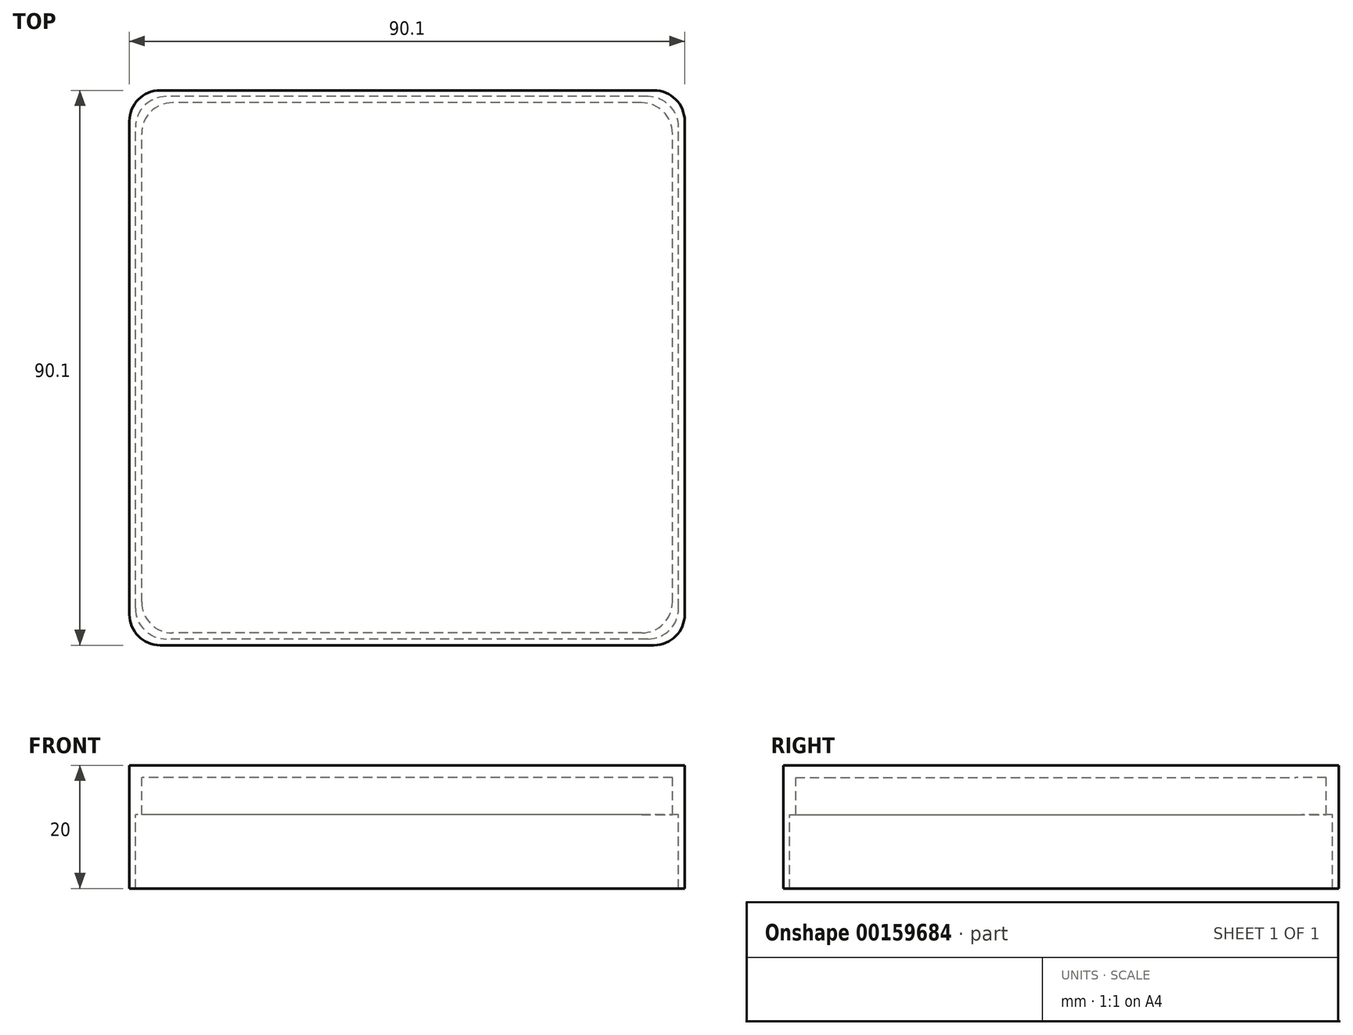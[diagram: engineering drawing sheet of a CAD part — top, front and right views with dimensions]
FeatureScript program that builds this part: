
annotation { "Feature Type Name" : "Feature", "Feature Type Description" : "" }
export const myFeature = defineFeature(function(context is Context, id is Id, definition is map)
    precondition{}
    {
        {
            var Q0;
            Q0=qCreatedBy(makeId("Top.planeOp"),FACE);
            var sketch = newSketch(context, id + "F0", { "sketchPlane" : qUnion([Q0])});
            skLineSegment(sketch, "E0.bottom", {"start": v(45.05, -45.05) * mm, "end": v(-45.05, -45.05) * mm});
            skLineSegment(sketch, "E0.top", {"start": v(45.05, 45.05) * mm, "end": v(-45.05, 45.05) * mm});
            skLineSegment(sketch, "E0.left", {"start": v(45.05, -45.05) * mm, "end": v(45.05, 45.05) * mm});
            skLineSegment(sketch, "E0.right", {"start": v(-45.05, -45.05) * mm, "end": v(-45.05, 45.05) * mm});
            skPoint(sketch, "E0.middle", {"position": v(0, 0) * mm});
            skLineSegment(sketch, "E1.bottom", {"start": v(44.05, -44.05) * mm, "end": v(-44.05, -44.05) * mm});
            skLineSegment(sketch, "E1.top", {"start": v(44.05, 44.05) * mm, "end": v(-44.05, 44.05) * mm});
            skLineSegment(sketch, "E1.left", {"start": v(44.05, -44.05) * mm, "end": v(44.05, 44.05) * mm});
            skLineSegment(sketch, "E1.right", {"start": v(-44.05, -44.05) * mm, "end": v(-44.05, 44.05) * mm});
            skLineSegment(sketch, "E2.bottom", {"start": v(43.05, -43.05) * mm, "end": v(-43.05, -43.05) * mm});
            skLineSegment(sketch, "E2.top", {"start": v(43.05, 43.05) * mm, "end": v(-43.05, 43.05) * mm});
            skLineSegment(sketch, "E2.left", {"start": v(43.05, -43.05) * mm, "end": v(43.05, 43.05) * mm});
            skLineSegment(sketch, "E2.right", {"start": v(-43.05, -43.05) * mm, "end": v(-43.05, 43.05) * mm});
            skSolve(sketch);
        }
        {
            var Q0;
            Q0=makeQuery(id+"F0.imprint","IMPRINT",FACE,{"disambiguationData":[TD([[makeQuery(id+"F0.imprint","IMPRINT",EDGE,{"derivedFrom":sQuery(id+"F0.wireOp",EDGE,"E2.bottom")}),-1.0]])]});
            extrude(context, id + "F1", {"entities" : qUnion([Q0]), "oppositeDirection" : true, "depth" : 2 * mm});
        }
        {
            var Q0;
            Q0=makeQuery(id+"F0.imprint","IMPRINT",FACE,{"disambiguationData":[TD([[makeQuery(id+"F0.imprint","IMPRINT",EDGE,{"derivedFrom":sQuery(id+"F0.wireOp",EDGE,"E1.bottom")}),-1.0]])]});
            extrude(context, id + "F2", {"entities" : qUnion([Q0]), "operationType" : NewBodyOperationType.ADD, "oppositeDirection" : true, "depth" : 8 * mm});
        }
        {
            var Q0;
            Q0=makeQuery(id+"F0.imprint","IMPRINT",FACE,{"disambiguationData":[TD([[makeQuery(id+"F0.imprint","IMPRINT",EDGE,{"derivedFrom":sQuery(id+"F0.wireOp",EDGE,"E0.bottom")}),-1.0]])]});
            extrude(context, id + "F3", {"entities" : qUnion([Q0]), "operationType" : NewBodyOperationType.ADD, "oppositeDirection" : true, "depth" : 20 * mm});
        }
        {
            var Q0;
            Q0=makeQuery(id+"F2.opExtrude","SWEPT_EDGE",EDGE,{"disambiguationData":[OSD([sQuery(id+"F0.wireOp",EDGE,"E2.bottom"),sQuery(id+"F0.wireOp",EDGE,"E2.right")])]});
            var Q1;
            Q1=makeQuery(id+"F3.opExtrude","SWEPT_EDGE",EDGE,{"disambiguationData":[OSD([sQuery(id+"F0.wireOp",EDGE,"E1.bottom"),sQuery(id+"F0.wireOp",EDGE,"E1.right")])]});
            var Q2;
            Q2=makeQuery(id+"F2.opExtrude","SWEPT_EDGE",EDGE,{"disambiguationData":[OSD([sQuery(id+"F0.wireOp",EDGE,"E2.bottom"),sQuery(id+"F0.wireOp",EDGE,"E2.left")])]});
            var Q3;
            Q3=makeQuery(id+"F3.opExtrude","SWEPT_EDGE",EDGE,{"disambiguationData":[OSD([sQuery(id+"F0.wireOp",EDGE,"E1.bottom"),sQuery(id+"F0.wireOp",EDGE,"E1.left")])]});
            var Q4;
            Q4=makeQuery(id+"F2.opExtrude","SWEPT_EDGE",EDGE,{"disambiguationData":[OSD([sQuery(id+"F0.wireOp",EDGE,"E2.top"),sQuery(id+"F0.wireOp",EDGE,"E2.left")])]});
            var Q5;
            Q5=makeQuery(id+"F3.opExtrude","SWEPT_EDGE",EDGE,{"disambiguationData":[OSD([sQuery(id+"F0.wireOp",EDGE,"E1.top"),sQuery(id+"F0.wireOp",EDGE,"E1.left")])]});
            var Q6;
            Q6=makeQuery(id+"F2.opExtrude","SWEPT_EDGE",EDGE,{"disambiguationData":[OSD([sQuery(id+"F0.wireOp",EDGE,"E2.top"),sQuery(id+"F0.wireOp",EDGE,"E2.right")])]});
            var Q7;
            Q7=makeQuery(id+"F3.opExtrude","SWEPT_EDGE",EDGE,{"disambiguationData":[OSD([sQuery(id+"F0.wireOp",EDGE,"E1.top"),sQuery(id+"F0.wireOp",EDGE,"E1.right")])]});
            var Q8;
            Q8=makeQuery(id+"F3.opExtrude","SWEPT_EDGE",EDGE,{"disambiguationData":[OSD([sQuery(id+"F0.wireOp",EDGE,"E0.bottom"),sQuery(id+"F0.wireOp",EDGE,"E0.left")])]});
            var Q9;
            Q9=makeQuery(id+"F3.opExtrude","SWEPT_EDGE",EDGE,{"disambiguationData":[OSD([sQuery(id+"F0.wireOp",EDGE,"E0.top"),sQuery(id+"F0.wireOp",EDGE,"E0.left")])]});
            var Q10;
            Q10=makeQuery(id+"F3.opExtrude","SWEPT_EDGE",EDGE,{"disambiguationData":[OSD([sQuery(id+"F0.wireOp",EDGE,"E0.bottom"),sQuery(id+"F0.wireOp",EDGE,"E0.right")])]});
            var Q11;
            Q11=makeQuery(id+"F3.opExtrude","SWEPT_EDGE",EDGE,{"disambiguationData":[OSD([sQuery(id+"F0.wireOp",EDGE,"E0.top"),sQuery(id+"F0.wireOp",EDGE,"E0.right")])]});
            fillet(context, id + "F4", {"entities" : qUnion([Q0, Q1, Q2, Q3, Q4, Q5, Q6, Q7, Q8, Q9, Q10, Q11]), "radius" : 5 * mm, "tangentPropagation" : true, "allowEdgeOverflow" : false});
        }
    });
